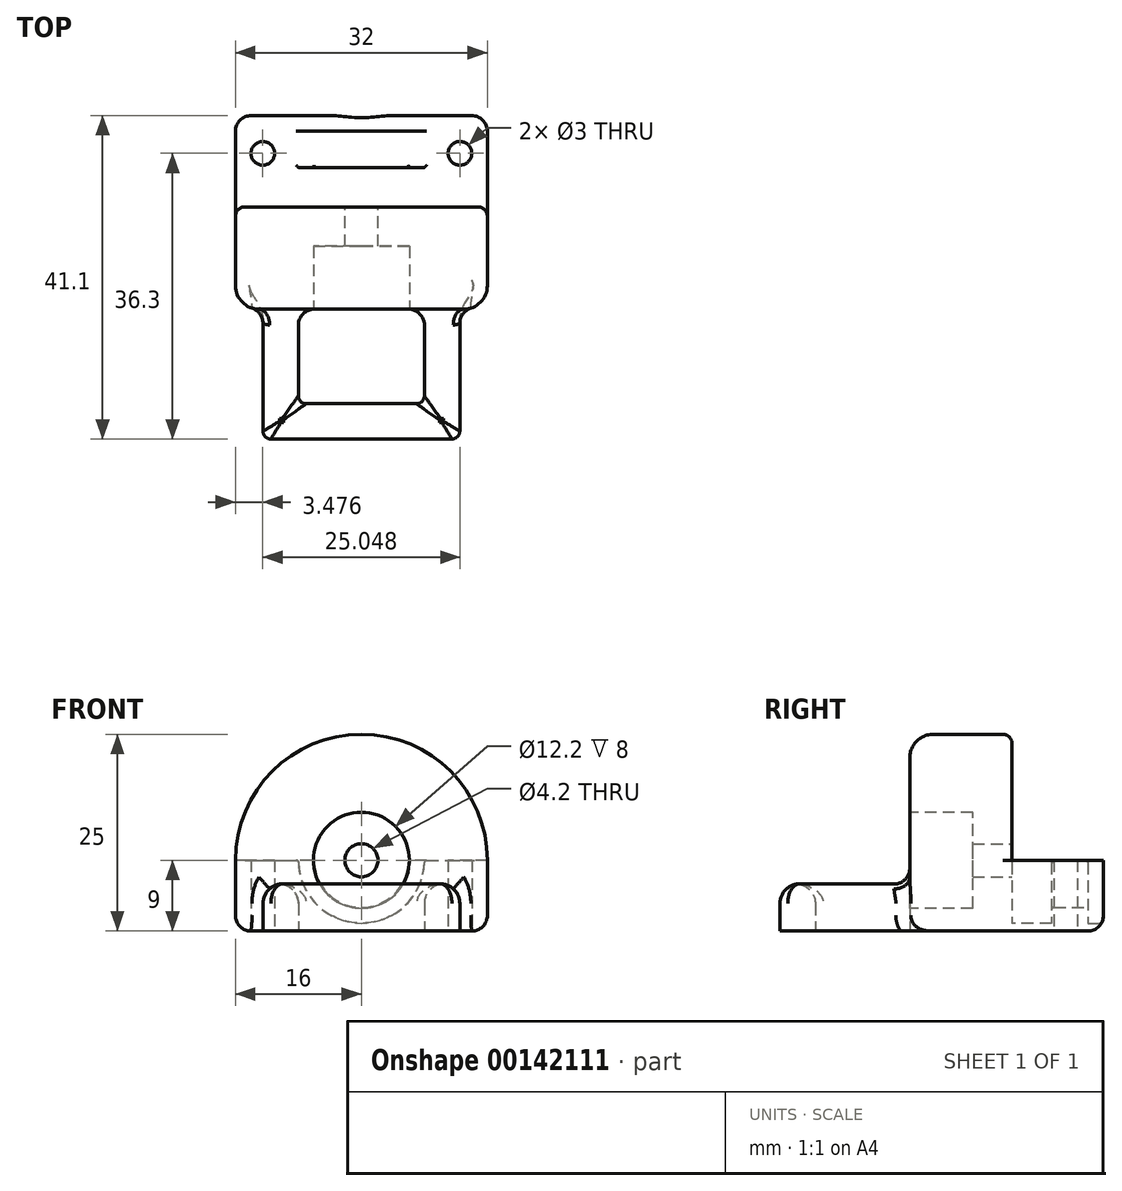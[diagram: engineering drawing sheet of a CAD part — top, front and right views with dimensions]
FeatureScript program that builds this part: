
annotation { "Feature Type Name" : "Feature", "Feature Type Description" : "" }
export const myFeature = defineFeature(function(context is Context, id is Id, definition is map)
    precondition{}
    {
        {
            var Q0;
            Q0=qCreatedBy(makeId("Top.planeOp"),FACE);
            var sketch = newSketch(context, id + "F0", { "sketchPlane" : qUnion([Q0])});
            skLineSegment(sketch, "E0.rect.bottom", {"start": v(-16, 5.8) * mm, "end": v(16, 5.8) * mm});
            skLineSegment(sketch, "E0.rect.top", {"start": v(-16, -5.8) * mm, "end": v(16, -5.8) * mm});
            skLineSegment(sketch, "E0.rect.left", {"start": v(-16, 5.8) * mm, "end": v(-16, -5.8) * mm});
            skLineSegment(sketch, "E0.rect.right", {"start": v(16, 5.8) * mm, "end": v(16, -5.8) * mm});
            skPoint(sketch, "E0.rect.middle", {"position": v(0, 0) * mm});
            skCircle(sketch, "E1", {"center": v(12.52, 1) * mm, "radius": 1.5 * mm});
            skCircle(sketch, "E2", {"center": v(-12.52, 1) * mm, "radius": 1.5 * mm});
            skSolve(sketch);
        }
        {
            var Q0;
            Q0=makeQuery(id+"F0.imprint","IMPRINT",FACE,{"disambiguationData":[TD([[makeQuery(id+"F0.imprint","IMPRINT",EDGE,{"derivedFrom":sQuery(id+"F0.wireOp",EDGE,"E0.rect.bottom")}),-1.0]])]});
            extrude(context, id + "F1", {"entities" : qUnion([Q0]), "depth" : 9 * mm});
        }
        {
            var Q0;
            Q0=makeQuery(id+"F1.opExtrude","SWEPT_FACE",FACE,{"disambiguationData":[OSD([sQuery(id+"F0.wireOp",EDGE,"E0.rect.top")])]});
            var sketch = newSketch(context, id + "F2", { "sketchPlane" : qUnion([Q0])});
            skCircle(sketch, "E3", {"center": v(0, 9) * mm, "radius": 8 * mm});
            skSolve(sketch);
        }
        {
            var Q0;
            Q0=qSketchRegion(id+"F2",true);
            var Q1;
            Q1=makeQuery(id+"F1.opExtrude","SWEPT_FACE",FACE,{"disambiguationData":[OSD([sQuery(id+"F0.wireOp",EDGE,"E0.rect.bottom")])]});
            extrude(context, id + "F3", {"entities" : qUnion([Q0, Q1]), "operationType" : NewBodyOperationType.REMOVE, "oppositeDirection" : true, "depth" : 5 * mm});
        }
        {
            var Q0;
            Q0=makeQuery(id+"F1.opExtrude","SWEPT_FACE",FACE,{"disambiguationData":[OSD([sQuery(id+"F0.wireOp",EDGE,"E0.rect.bottom")])]});
            var sketch = newSketch(context, id + "F4", { "sketchPlane" : qUnion([Q0])});
            skCircle(sketch, "E4", {"center": v(0, 9) * mm, "radius": 8 * mm});
            skSolve(sketch);
        }
        {
            var Q0;
            Q0=qSketchRegion(id+"F4",true);
            extrude(context, id + "F5", {"entities" : qUnion([Q0]), "operationType" : NewBodyOperationType.REMOVE, "oppositeDirection" : true, "depth" : 2 * mm});
        }
        {
            var Q0;
            Q0=makeQuery(id+"F5.boolean.opBoolean","COPY",FACE,{"derivedFrom":makeQuery(id+"F5.opExtrude","CAP_FACE",FACE,{"disambiguationData":[OSD([sQuery(id+"F4.wireOp",EDGE,"E4")])],"isStart":false})});
            var sketch = newSketch(context, id + "F6", { "sketchPlane" : qUnion([Q0])});
            skCircle(sketch, "E5", {"center": v(0, 9) * mm, "radius": 6 * mm});
            skSolve(sketch);
        }
        {
            var Q0;
            Q0=qSketchRegion(id+"F6",true);
            extrude(context, id + "F7", {"entities" : qUnion([Q0]), "operationType" : NewBodyOperationType.REMOVE, "oppositeDirection" : true, "depth" : 25 * mm});
        }
        {
            var Q0;
            Q0=makeQuery(id+"F1.opExtrude","SWEPT_FACE",FACE,{"disambiguationData":[OSD([sQuery(id+"F0.wireOp",EDGE,"E0.rect.top")])]});
            var sketch = newSketch(context, id + "F8", { "sketchPlane" : qUnion([Q0])});
            skArc(sketch, "E6", {"start": v(16, 9) * mm, "mid": v(0, 25) * mm, "end": v(-16, 9) * mm});
            skLineSegment(sketch, "E7", {"start": v(0, 0) * mm, "end": v(13.23, 0) * mm});
            skLineSegment(sketch, "E8", {"start": v(-13.23, 0) * mm, "end": v(0, 0) * mm});
            skLineSegment(sketch, "E9", {"start": v(-16, 9) * mm, "end": v(-16, 0) * mm});
            skLineSegment(sketch, "E10", {"start": v(16, 9) * mm, "end": v(16, 0) * mm});
            skLineSegment(sketch, "E11", {"start": v(-16, 0) * mm, "end": v(16, 0) * mm});
            skSolve(sketch);
        }
        {
            var Q0;
            Q0=qSketchRegion(id+"F8",true);
            extrude(context, id + "F9", {"entities" : qUnion([Q0]), "operationType" : NewBodyOperationType.ADD, "depth" : 13 * mm});
        }
        {
            var Q0;
            Q0=qCreatedBy(makeId("Top.planeOp"),FACE);
            var sketch = newSketch(context, id + "F10", { "sketchPlane" : qUnion([Q0])});
            skLineSegment(sketch, "E12", {"start": v(-8, -18.8) * mm, "end": v(-12.5, -18.8) * mm});
            skLineSegment(sketch, "E13", {"start": v(-12.5, -18.8) * mm, "end": v(-8, -18.8) * mm});
            skLineSegment(sketch, "E14", {"start": v(12.5, -18.8) * mm, "end": v(12.5, -35.3) * mm});
            skLineSegment(sketch, "E15", {"start": v(12.5, -35.3) * mm, "end": v(-12.5, -35.3) * mm});
            skLineSegment(sketch, "E16", {"start": v(-12.5, -35.3) * mm, "end": v(-12.5, -18.8) * mm});
            skLineSegment(sketch, "E17", {"start": v(-8, -18.8) * mm, "end": v(-8, -30.8) * mm});
            skLineSegment(sketch, "E18", {"start": v(-8, -30.8) * mm, "end": v(8, -30.8) * mm});
            skLineSegment(sketch, "E19", {"start": v(8, -30.8) * mm, "end": v(8, -18.8) * mm});
            skLineSegment(sketch, "E20.trimOffspring", {"start": v(8, -18.8) * mm, "end": v(12.5, -18.8) * mm});
            skPoint(sketch, "E21.orphan", {"position": v(0, -18.8) * mm});
            skPoint(sketch, "E22", {"position": v(0, -30.8) * mm});
            skPoint(sketch, "E23", {"position": v(0, -35.3) * mm});
            skSolve(sketch);
        }
        {
            var Q0;
            Q0=qSketchRegion(id+"F10",true);
            extrude(context, id + "F11", {"entities" : qUnion([Q0]), "operationType" : NewBodyOperationType.ADD, "depth" : 6 * mm});
        }
        {
            var Q0;
            Q0=makeQuery(id+"F11.opExtrude","CAP_EDGE",EDGE,{"disambiguationData":[OSD([sQuery(id+"F10.wireOp",EDGE,"E17")])],"isStart":false});
            var Q1;
            Q1=makeQuery(id+"F11.opExtrude","CAP_EDGE",EDGE,{"disambiguationData":[OSD([sQuery(id+"F10.wireOp",EDGE,"E16")])],"isStart":false});
            var Q2;
            Q2=makeQuery(id+"F11.opExtrude","CAP_EDGE",EDGE,{"disambiguationData":[OSD([sQuery(id+"F10.wireOp",EDGE,"E19")])],"isStart":false});
            var Q3;
            Q3=makeQuery(id+"F11.opExtrude","CAP_EDGE",EDGE,{"disambiguationData":[OSD([sQuery(id+"F10.wireOp",EDGE,"E14")])],"isStart":false});
            var Q4;
            Q4=makeQuery(id+"F11.opExtrude","CAP_EDGE",EDGE,{"disambiguationData":[OSD([sQuery(id+"F10.wireOp",EDGE,"E18")])],"isStart":false});
            var Q5;
            Q5=makeQuery(id+"F11.opExtrude","CAP_EDGE",EDGE,{"disambiguationData":[OSD([sQuery(id+"F10.wireOp",EDGE,"E15")])],"isStart":false});
            fillet(context, id + "F12", {"entities" : qUnion([Q0, Q1, Q2, Q3, Q4, Q5]), "radius" : 2.5 * mm, "tangentPropagation" : true, "allowEdgeOverflow" : false});
        }
        {
            var Q0;
            Q0=makeQuery(id+"F9.opExtrude","CAP_EDGE",EDGE,{"disambiguationData":[OSD([sQuery(id+"F8.wireOp",EDGE,"E6")])],"isStart":false});
            fillet(context, id + "F13", {"entities" : qUnion([Q0]), "radius" : 3 * mm, "tangentPropagation" : true, "allowEdgeOverflow" : false});
        }
        {
            var Q0;
            Q0=makeQuery(id+"F9.opExtrude","CAP_EDGE",EDGE,{"disambiguationData":[OSD([sQuery(id+"F8.wireOp",EDGE,"E6")])],"isStart":true});
            fillet(context, id + "F14", {"entities" : qUnion([Q0]), "radius" : 1.2 * mm, "tangentPropagation" : true, "allowEdgeOverflow" : false});
        }
        {
            var Q0;
            Q0=makeQuery(id+"F9.opExtrude","CAP_FACE",FACE,{"disambiguationData":[OSD([sQuery(id+"F8.wireOp",EDGE,"E6"),sQuery(id+"F8.wireOp",EDGE,"E9"),sQuery(id+"F8.wireOp",EDGE,"E10"),sQuery(id+"F8.wireOp",EDGE,"E11")])],"isStart":false});
            var sketch = newSketch(context, id + "F15", { "sketchPlane" : qUnion([Q0])});
            skCircle(sketch, "E24", {"center": v(0, 9) * mm, "radius": 6.1 * mm});
            skSolve(sketch);
        }
        {
            var Q0;
            Q0=qSketchRegion(id+"F15",true);
            extrude(context, id + "F16", {"entities" : qUnion([Q0]), "operationType" : NewBodyOperationType.REMOVE, "oppositeDirection" : true, "depth" : 8 * mm});
        }
        {
            var Q0;
            Q0=makeQuery(id+"F13.opFillet","BLEND_EDGE",EDGE,{"blendedFrom":[makeQuery(id+"F9.opExtrude","CAP_EDGE",EDGE,{"disambiguationData":[OSD([sQuery(id+"F8.wireOp",EDGE,"E9")])],"isStart":false}),makeQuery(id+"F9.boolean.opBoolean","MERGE",FACE,{"derivedFrom":[makeQuery(id+"F1.opExtrude","CAP_FACE",FACE,{"disambiguationData":[OSD([sQuery(id+"F0.wireOp",EDGE,"E0.rect.bottom"),sQuery(id+"F0.wireOp",EDGE,"E0.rect.top"),sQuery(id+"F0.wireOp",EDGE,"E0.rect.left"),sQuery(id+"F0.wireOp",EDGE,"E0.rect.right"),sQuery(id+"F0.wireOp",EDGE,"E1"),sQuery(id+"F0.wireOp",EDGE,"E2")])],"isStart":true}),makeQuery(id+"F9.opExtrude","SWEPT_FACE",FACE,{"disambiguationData":[OSD([sQuery(id+"F8.wireOp",EDGE,"E11")])]})]})],"blendedInto":[makeQuery(id+"F9.boolean.opBoolean","MERGE",FACE,{"derivedFrom":[makeQuery(id+"F1.opExtrude","CAP_FACE",FACE,{"disambiguationData":[OSD([sQuery(id+"F0.wireOp",EDGE,"E0.rect.bottom"),sQuery(id+"F0.wireOp",EDGE,"E0.rect.top"),sQuery(id+"F0.wireOp",EDGE,"E0.rect.left"),sQuery(id+"F0.wireOp",EDGE,"E0.rect.right"),sQuery(id+"F0.wireOp",EDGE,"E1"),sQuery(id+"F0.wireOp",EDGE,"E2")])],"isStart":true}),makeQuery(id+"F9.opExtrude","SWEPT_FACE",FACE,{"disambiguationData":[OSD([sQuery(id+"F8.wireOp",EDGE,"E11")])]})]})]});
            fillet(context, id + "F17", {"entities" : qUnion([Q0]), "radius" : 2 * mm, "tangentPropagation" : true, "allowEdgeOverflow" : false});
        }
        {
            var Q0;
            {var subQ0=sQuery(id+"F8.wireOp",EDGE,"E6");var subQ1=sQuery(id+"F8.wireOp",EDGE,"E9");var subQ2=sQuery(id+"F8.wireOp",EDGE,"E10");Q0=makeQuery(id+"F9.boolean.opBoolean","SPLIT",FACE,{"disambiguationData":[TD([makeQuery(id+"F3.boolean.opBoolean","COPY",FACE,{"derivedFrom":makeQuery(id+"F3.opExtrude","SWEPT_FACE",FACE,{"disambiguationData":[OSD([sQuery(id+"F2.wireOp",EDGE,"E3")])]})})])],"derivedFrom":makeQuery(id+"F9.opExtrude","CAP_FACE",FACE,{"disambiguationData":[OSD([subQ0,subQ1,subQ2,sQuery(id+"F8.wireOp",EDGE,"E11")])],"isStart":true})});}
            var sketch = newSketch(context, id + "F18", { "sketchPlane" : qUnion([Q0])});
            skCircle(sketch, "E25", {"center": v(0, 9) * mm, "radius": 2.1 * mm});
            skSolve(sketch);
        }
        {
            var Q0;
            Q0=makeQuery(id+"F1.opExtrude","CAP_EDGE",EDGE,{"disambiguationData":[OSD([sQuery(id+"F0.wireOp",EDGE,"E0.rect.bottom")])],"isStart":true});
            var Q1;
            Q1=makeQuery(id+"F7.boolean.opBoolean","COPY",EDGE,{"derivedFrom":makeQuery(id+"F7.opExtrude","CAP_EDGE",EDGE,{"disambiguationData":[OSD([sQuery(id+"F6.wireOp",EDGE,"E5")])],"isStart":true})});
            var Q2;
            Q2=makeQuery(id+"F1.opExtrude","SWEPT_EDGE",EDGE,{"disambiguationData":[OSD([sQuery(id+"F0.wireOp",EDGE,"E0.rect.bottom"),sQuery(id+"F0.wireOp",EDGE,"E0.rect.left")])]});
            var Q3;
            Q3=makeQuery(id+"F1.opExtrude","CAP_EDGE",EDGE,{"disambiguationData":[OSD([sQuery(id+"F0.wireOp",EDGE,"E0.rect.left")])],"isStart":true});
            var Q4;
            Q4=makeQuery(id+"F1.opExtrude","SWEPT_EDGE",EDGE,{"disambiguationData":[OSD([sQuery(id+"F0.wireOp",EDGE,"E0.rect.bottom"),sQuery(id+"F0.wireOp",EDGE,"E0.rect.right")])]});
            var Q5;
            Q5=makeQuery(id+"F1.opExtrude","CAP_EDGE",EDGE,{"disambiguationData":[OSD([sQuery(id+"F0.wireOp",EDGE,"E0.rect.right")])],"isStart":true});
            fillet(context, id + "F19", {"entities" : qUnion([Q0, Q1, Q2, Q3, Q4, Q5]), "radius" : 2 * mm, "tangentPropagation" : true, "allowEdgeOverflow" : false});
        }
        {
            var Q0;
            Q0=qSketchRegion(id+"F18",true);
            extrude(context, id + "F20", {"entities" : qUnion([Q0]), "operationType" : NewBodyOperationType.REMOVE, "oppositeDirection" : true, "depth" : 7 * mm});
        }
        {
            var Q0;
            Q0=makeQuery(id+"F12.opFillet","BLEND_EDGE",EDGE,{"blendedFrom":[makeQuery(id+"F11.opExtrude","CAP_EDGE",EDGE,{"disambiguationData":[OSD([sQuery(id+"F10.wireOp",EDGE,"E14")])],"isStart":false}),makeQuery(id+"F11.opExtrude","CAP_EDGE",EDGE,{"disambiguationData":[OSD([sQuery(id+"F10.wireOp",EDGE,"E15")])],"isStart":false})],"blendedInto":[]});
            var Q1;
            Q1=makeQuery(id+"F12.opFillet","BLEND_EDGE",EDGE,{"blendedFrom":[makeQuery(id+"F11.opExtrude","CAP_EDGE",EDGE,{"disambiguationData":[OSD([sQuery(id+"F10.wireOp",EDGE,"E18")])],"isStart":false}),makeQuery(id+"F11.opExtrude","CAP_EDGE",EDGE,{"disambiguationData":[OSD([sQuery(id+"F10.wireOp",EDGE,"E19")])],"isStart":false})],"blendedInto":[]});
            var Q2;
            Q2=makeQuery(id+"F12.opFillet","BLEND_EDGE",EDGE,{"blendedFrom":[makeQuery(id+"F11.opExtrude","CAP_EDGE",EDGE,{"disambiguationData":[OSD([sQuery(id+"F10.wireOp",EDGE,"E14")])],"isStart":false}),makeQuery(id+"F11.opExtrude","CAP_EDGE",EDGE,{"disambiguationData":[OSD([sQuery(id+"F10.wireOp",EDGE,"E19")])],"isStart":false})],"blendedInto":[]});
            var Q3;
            Q3=makeQuery(id+"F12.opFillet","BLEND_EDGE",EDGE,{"blendedFrom":[makeQuery(id+"F11.opExtrude","CAP_EDGE",EDGE,{"disambiguationData":[OSD([sQuery(id+"F10.wireOp",EDGE,"E15")])],"isStart":false}),makeQuery(id+"F11.opExtrude","CAP_EDGE",EDGE,{"disambiguationData":[OSD([sQuery(id+"F10.wireOp",EDGE,"E18")])],"isStart":false})],"blendedInto":[]});
            var Q4;
            Q4=makeQuery(id+"F12.opFillet","BLEND_EDGE",EDGE,{"blendedFrom":[makeQuery(id+"F11.opExtrude","CAP_EDGE",EDGE,{"disambiguationData":[OSD([sQuery(id+"F10.wireOp",EDGE,"E16")])],"isStart":false}),makeQuery(id+"F11.opExtrude","CAP_EDGE",EDGE,{"disambiguationData":[OSD([sQuery(id+"F10.wireOp",EDGE,"E17")])],"isStart":false})],"blendedInto":[]});
            var Q5;
            Q5=makeQuery(id+"F12.opFillet","BLEND_EDGE",EDGE,{"blendedFrom":[makeQuery(id+"F11.opExtrude","CAP_EDGE",EDGE,{"disambiguationData":[OSD([sQuery(id+"F10.wireOp",EDGE,"E15")])],"isStart":false}),makeQuery(id+"F11.opExtrude","CAP_EDGE",EDGE,{"disambiguationData":[OSD([sQuery(id+"F10.wireOp",EDGE,"E16")])],"isStart":false})],"blendedInto":[]});
            var Q6;
            Q6=makeQuery(id+"F12.opFillet","BLEND_EDGE",EDGE,{"blendedFrom":[makeQuery(id+"F11.opExtrude","CAP_EDGE",EDGE,{"disambiguationData":[OSD([sQuery(id+"F10.wireOp",EDGE,"E17")])],"isStart":false}),makeQuery(id+"F11.opExtrude","CAP_EDGE",EDGE,{"disambiguationData":[OSD([sQuery(id+"F10.wireOp",EDGE,"E18")])],"isStart":false})],"blendedInto":[]});
            fillet(context, id + "F21", {"entities" : qUnion([Q0, Q1, Q2, Q3, Q4, Q5, Q6]), "radius" : 1 * mm, "tangentPropagation" : true, "allowEdgeOverflow" : false});
        }
        {
            var Q0;
            Q0=makeQuery(id+"F12.opFillet","BLEND_EDGE",EDGE,{"blendedFrom":[makeQuery(id+"F11.opExtrude","CAP_EDGE",EDGE,{"disambiguationData":[OSD([sQuery(id+"F10.wireOp",EDGE,"E14")])],"isStart":false}),makeQuery(id+"F9.opExtrude","CAP_FACE",FACE,{"disambiguationData":[OSD([sQuery(id+"F8.wireOp",EDGE,"E6"),sQuery(id+"F8.wireOp",EDGE,"E9"),sQuery(id+"F8.wireOp",EDGE,"E10"),sQuery(id+"F8.wireOp",EDGE,"E11")])],"isStart":false})],"blendedInto":[makeQuery(id+"F9.opExtrude","CAP_FACE",FACE,{"disambiguationData":[OSD([sQuery(id+"F8.wireOp",EDGE,"E6"),sQuery(id+"F8.wireOp",EDGE,"E9"),sQuery(id+"F8.wireOp",EDGE,"E10"),sQuery(id+"F8.wireOp",EDGE,"E11")])],"isStart":false})]});
            var Q1;
            Q1=makeQuery(id+"F12.opFillet","BLEND_EDGE",EDGE,{"blendedFrom":[makeQuery(id+"F11.opExtrude","CAP_EDGE",EDGE,{"disambiguationData":[OSD([sQuery(id+"F10.wireOp",EDGE,"E17")])],"isStart":false}),makeQuery(id+"F9.opExtrude","CAP_FACE",FACE,{"disambiguationData":[OSD([sQuery(id+"F8.wireOp",EDGE,"E6"),sQuery(id+"F8.wireOp",EDGE,"E9"),sQuery(id+"F8.wireOp",EDGE,"E10"),sQuery(id+"F8.wireOp",EDGE,"E11")])],"isStart":false})],"blendedInto":[makeQuery(id+"F9.opExtrude","CAP_FACE",FACE,{"disambiguationData":[OSD([sQuery(id+"F8.wireOp",EDGE,"E6"),sQuery(id+"F8.wireOp",EDGE,"E9"),sQuery(id+"F8.wireOp",EDGE,"E10"),sQuery(id+"F8.wireOp",EDGE,"E11")])],"isStart":false})]});
            fillet(context, id + "F22", {"entities" : qUnion([Q0, Q1]), "radius" : 2 * mm, "tangentPropagation" : true, "allowEdgeOverflow" : false});
        }
        {
            var Q0;
            Q0=makeQuery(id+"F3.boolean.opBoolean","INTERSECT",EDGE,{"disambiguationData":[OD(0.0)],"derivedFrom":[makeQuery(id+"F1.opExtrude","CAP_FACE",FACE,{"disambiguationData":[OSD([sQuery(id+"F0.wireOp",EDGE,"E0.rect.bottom"),sQuery(id+"F0.wireOp",EDGE,"E0.rect.top"),sQuery(id+"F0.wireOp",EDGE,"E0.rect.left"),sQuery(id+"F0.wireOp",EDGE,"E0.rect.right"),sQuery(id+"F0.wireOp",EDGE,"E1"),sQuery(id+"F0.wireOp",EDGE,"E2")])],"isStart":false}),makeQuery(id+"F3.opExtrude","SWEPT_FACE",FACE,{"disambiguationData":[OSD([sQuery(id+"F2.wireOp",EDGE,"E3")])]})]});
            var Q1;
            Q1=makeQuery(id+"F3.boolean.opBoolean","INTERSECT",EDGE,{"disambiguationData":[OD(1.0)],"derivedFrom":[makeQuery(id+"F1.opExtrude","CAP_FACE",FACE,{"disambiguationData":[OSD([sQuery(id+"F0.wireOp",EDGE,"E0.rect.bottom"),sQuery(id+"F0.wireOp",EDGE,"E0.rect.top"),sQuery(id+"F0.wireOp",EDGE,"E0.rect.left"),sQuery(id+"F0.wireOp",EDGE,"E0.rect.right"),sQuery(id+"F0.wireOp",EDGE,"E1"),sQuery(id+"F0.wireOp",EDGE,"E2")])],"isStart":false}),makeQuery(id+"F3.opExtrude","SWEPT_FACE",FACE,{"disambiguationData":[OSD([sQuery(id+"F2.wireOp",EDGE,"E3")])]})]});
            var Q2;
            Q2=makeQuery(id+"F7.boolean.opBoolean","INTERSECT",EDGE,{"disambiguationData":[OD(1.0)],"derivedFrom":[makeQuery(id+"F1.opExtrude","CAP_FACE",FACE,{"disambiguationData":[OSD([sQuery(id+"F0.wireOp",EDGE,"E0.rect.bottom"),sQuery(id+"F0.wireOp",EDGE,"E0.rect.top"),sQuery(id+"F0.wireOp",EDGE,"E0.rect.left"),sQuery(id+"F0.wireOp",EDGE,"E0.rect.right"),sQuery(id+"F0.wireOp",EDGE,"E1"),sQuery(id+"F0.wireOp",EDGE,"E2")])],"isStart":false}),makeQuery(id+"F7.opExtrude","SWEPT_FACE",FACE,{"disambiguationData":[OSD([sQuery(id+"F6.wireOp",EDGE,"E5")])]})]});
            var Q3;
            Q3=makeQuery(id+"F7.boolean.opBoolean","INTERSECT",EDGE,{"disambiguationData":[OD(0.0)],"derivedFrom":[makeQuery(id+"F1.opExtrude","CAP_FACE",FACE,{"disambiguationData":[OSD([sQuery(id+"F0.wireOp",EDGE,"E0.rect.bottom"),sQuery(id+"F0.wireOp",EDGE,"E0.rect.top"),sQuery(id+"F0.wireOp",EDGE,"E0.rect.left"),sQuery(id+"F0.wireOp",EDGE,"E0.rect.right"),sQuery(id+"F0.wireOp",EDGE,"E1"),sQuery(id+"F0.wireOp",EDGE,"E2")])],"isStart":false}),makeQuery(id+"F7.opExtrude","SWEPT_FACE",FACE,{"disambiguationData":[OSD([sQuery(id+"F6.wireOp",EDGE,"E5")])]})]});
            var Q4;
            Q4=makeQuery(id+"F5.boolean.opBoolean","INTERSECT",EDGE,{"disambiguationData":[OD(1.0)],"derivedFrom":[makeQuery(id+"F1.opExtrude","CAP_FACE",FACE,{"disambiguationData":[OSD([sQuery(id+"F0.wireOp",EDGE,"E0.rect.bottom"),sQuery(id+"F0.wireOp",EDGE,"E0.rect.top"),sQuery(id+"F0.wireOp",EDGE,"E0.rect.left"),sQuery(id+"F0.wireOp",EDGE,"E0.rect.right"),sQuery(id+"F0.wireOp",EDGE,"E1"),sQuery(id+"F0.wireOp",EDGE,"E2")])],"isStart":false}),makeQuery(id+"F5.opExtrude","SWEPT_FACE",FACE,{"disambiguationData":[OSD([sQuery(id+"F4.wireOp",EDGE,"E4")])]})]});
            var Q5;
            Q5=makeQuery(id+"F5.boolean.opBoolean","INTERSECT",EDGE,{"disambiguationData":[OD(0.0)],"derivedFrom":[makeQuery(id+"F1.opExtrude","CAP_FACE",FACE,{"disambiguationData":[OSD([sQuery(id+"F0.wireOp",EDGE,"E0.rect.bottom"),sQuery(id+"F0.wireOp",EDGE,"E0.rect.top"),sQuery(id+"F0.wireOp",EDGE,"E0.rect.left"),sQuery(id+"F0.wireOp",EDGE,"E0.rect.right"),sQuery(id+"F0.wireOp",EDGE,"E1"),sQuery(id+"F0.wireOp",EDGE,"E2")])],"isStart":false}),makeQuery(id+"F5.opExtrude","SWEPT_FACE",FACE,{"disambiguationData":[OSD([sQuery(id+"F4.wireOp",EDGE,"E4")])]})]});
            var Q6;
            Q6=makeQuery(id+"F7.boolean.opBoolean","INTERSECT",EDGE,{"derivedFrom":[makeQuery(id+"F3.boolean.opBoolean","COPY",FACE,{"derivedFrom":makeQuery(id+"F3.opExtrude","CAP_FACE",FACE,{"disambiguationData":[OSD([sQuery(id+"F2.wireOp",EDGE,"E3")])],"isStart":false})}),makeQuery(id+"F7.opExtrude","SWEPT_FACE",FACE,{"disambiguationData":[OSD([sQuery(id+"F6.wireOp",EDGE,"E5")])]})]});
            var Q7;
            Q7=makeQuery(id+"F7.boolean.opBoolean","SPLIT",EDGE,{"disambiguationData":[OD(0.0)],"derivedFrom":makeQuery(id+"F3.boolean.opBoolean","INTERSECT",EDGE,{"derivedFrom":[makeQuery(id+"F1.opExtrude","CAP_FACE",FACE,{"disambiguationData":[OSD([sQuery(id+"F0.wireOp",EDGE,"E0.rect.bottom"),sQuery(id+"F0.wireOp",EDGE,"E0.rect.top"),sQuery(id+"F0.wireOp",EDGE,"E0.rect.left"),sQuery(id+"F0.wireOp",EDGE,"E0.rect.right"),sQuery(id+"F0.wireOp",EDGE,"E1"),sQuery(id+"F0.wireOp",EDGE,"E2")])],"isStart":false}),makeQuery(id+"F3.opExtrude","CAP_FACE",FACE,{"disambiguationData":[OSD([sQuery(id+"F2.wireOp",EDGE,"E3")])],"isStart":false})]})});
            var Q8;
            Q8=makeQuery(id+"F7.boolean.opBoolean","SPLIT",EDGE,{"disambiguationData":[OD(1.0)],"derivedFrom":makeQuery(id+"F3.boolean.opBoolean","INTERSECT",EDGE,{"derivedFrom":[makeQuery(id+"F1.opExtrude","CAP_FACE",FACE,{"disambiguationData":[OSD([sQuery(id+"F0.wireOp",EDGE,"E0.rect.bottom"),sQuery(id+"F0.wireOp",EDGE,"E0.rect.top"),sQuery(id+"F0.wireOp",EDGE,"E0.rect.left"),sQuery(id+"F0.wireOp",EDGE,"E0.rect.right"),sQuery(id+"F0.wireOp",EDGE,"E1"),sQuery(id+"F0.wireOp",EDGE,"E2")])],"isStart":false}),makeQuery(id+"F3.opExtrude","CAP_FACE",FACE,{"disambiguationData":[OSD([sQuery(id+"F2.wireOp",EDGE,"E3")])],"isStart":false})]})});
            var Q9;
            Q9=makeQuery(id+"F20.boolean.opBoolean","COPY",EDGE,{"derivedFrom":makeQuery(id+"F20.opExtrude","CAP_EDGE",EDGE,{"disambiguationData":[OSD([sQuery(id+"F18.wireOp",EDGE,"E25")])],"isStart":true})});
            fillet(context, id + "F23", {"entities" : qUnion([Q0, Q1, Q2, Q3, Q4, Q5, Q6, Q7, Q8, Q9]), "radius" : 0.3 * mm, "allowEdgeOverflow" : false});
        }
    });
